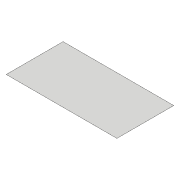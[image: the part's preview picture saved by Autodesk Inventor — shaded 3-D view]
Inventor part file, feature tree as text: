
AUTODESK INVENTOR PART (.ipt)
format: ipt  version: 2017 (Build 210142000, 142)  size: 69,120 bytes
history: native  units: mm
features: extrude x1, sketch x1
ambient origin geometry x8: Origin, YZ Plane, XZ Plane, XY Plane, X Axis, Y Axis, Z Axis, Center Point
bodies: Solid1 (feature_tree)
feature tree (2):
  extrude  "Extrusion1"  [1 undecoded]
  sketch  "Sketch1"  dims[d0=1.0mm d1=0.0mm]
note: 1 required parameter value undecoded (feature->parameter linkage not recoverable at this tier; creation-order binding heuristic only, values carry confidence <= 0.55)
